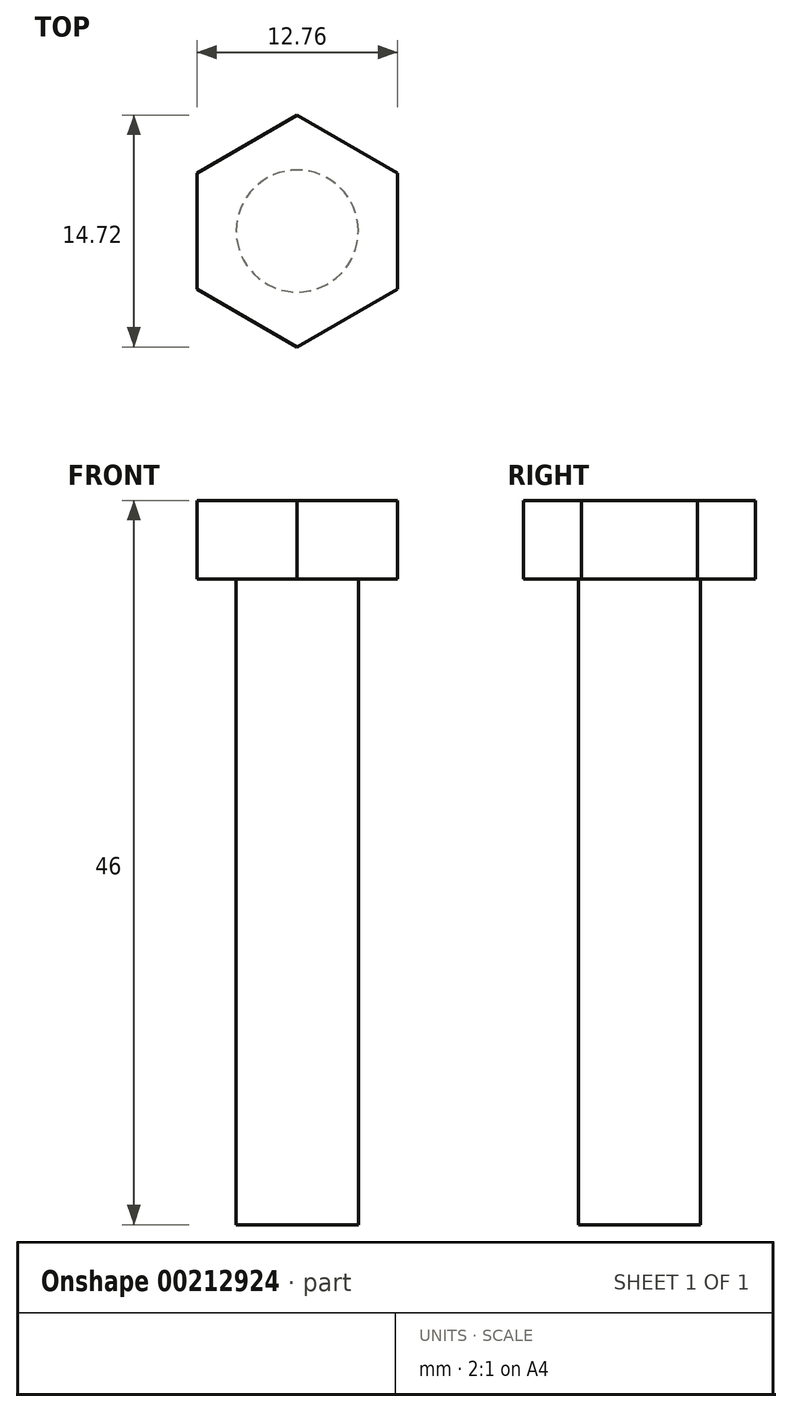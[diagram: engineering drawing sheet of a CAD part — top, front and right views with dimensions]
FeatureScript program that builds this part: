
annotation { "Feature Type Name" : "Feature", "Feature Type Description" : "" }
export const myFeature = defineFeature(function(context is Context, id is Id, definition is map)
    precondition{}
    {
        {
            var Q0;
            Q0=qCreatedBy(makeId("Top.planeOp"),FACE);
            var sketch = newSketch(context, id + "F0", { "sketchPlane" : qUnion([Q0])});
            skCircle(sketch, "E0.cCircle", {"center": v(0, 0) * mm, "radius": 6.38 * mm, "construction": true});
            skLineSegment(sketch, "E0.0", {"start": v(6.38, 3.68) * mm, "end": v(6.38, -3.68) * mm});
            skLineSegment(sketch, "E0.1", {"start": v(6.38, -3.68) * mm, "end": v(0, -7.36) * mm});
            skLineSegment(sketch, "E0.2", {"start": v(0, -7.36) * mm, "end": v(-6.37, -3.68) * mm});
            skLineSegment(sketch, "E0.3", {"start": v(-6.37, -3.68) * mm, "end": v(-6.38, 3.68) * mm});
            skLineSegment(sketch, "E0.4", {"start": v(-6.38, 3.68) * mm, "end": v(0, 7.36) * mm});
            skLineSegment(sketch, "E0.5", {"start": v(0, 7.36) * mm, "end": v(6.37, 3.68) * mm});
            skPoint(sketch, "E0.0.midPoint", {"position": v(6.38, 0) * mm});
            skSolve(sketch);
        }
        {
            var Q0;
            Q0 = qSketchRegion(id + "F0", true);
            var Q1;
            Q1=makeQuery(id+"F0.imprint","IMPRINT",FACE,{"disambiguationData":[TD([[makeQuery(id+"F0.imprint","IMPRINT",EDGE,{"derivedFrom":sQuery(id+"F0.wireOp",EDGE,"E0.0")}),-1.0]])]});
            extrude(context, id + "F1", {"entities" : qUnion([Q0, Q1]), "depth" : 5 * mm});
        }
        {
            var Q0;
            Q0=makeQuery(id+"F1.opExtrude","CAP_FACE",FACE,{"disambiguationData":[OSD([sQuery(id+"F0.wireOp",EDGE,"E0.0"),sQuery(id+"F0.wireOp",EDGE,"E0.1"),sQuery(id+"F0.wireOp",EDGE,"E0.2"),sQuery(id+"F0.wireOp",EDGE,"E0.3"),sQuery(id+"F0.wireOp",EDGE,"E0.4"),sQuery(id+"F0.wireOp",EDGE,"E0.5")])],"isStart":true});
            var sketch = newSketch(context, id + "F2", { "sketchPlane" : qUnion([Q0])});
            skCircle(sketch, "E1", {"center": v(0, 0) * mm, "radius": 3.88 * mm});
            skSolve(sketch);
        }
        {
            var Q0;
            Q0 = qSketchRegion(id + "F2", true);
            extrude(context, id + "F3", {"entities" : qUnion([Q0]), "operationType" : NewBodyOperationType.ADD, "depth" : 41 * mm});
        }
    });
